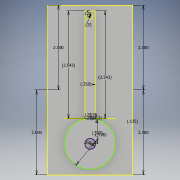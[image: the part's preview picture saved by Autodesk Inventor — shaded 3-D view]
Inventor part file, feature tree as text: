
AUTODESK INVENTOR PART (.ipt)
format: ipt  version: 2017 (Build 210142000, 142)  size: 172,032 bytes
history: native  units: in
note: dims shown in document units (in); Inventor stores cm internally (conversion verified against a paired STEP export)
features: sketch x12, extrude x5, hole x2, projected_geometry x2, plane x1
ambient origin geometry x8: Origin, YZ Plane, XZ Plane, XY Plane, X Axis, Y Axis, Z Axis, Center Point
bodies: Solid1 (feature_tree)
feature tree (22):
  extrude  "Extrusion1"  Depth=0.125in
  sketch  "Sketch2"  dims[d1=0.125in d2=0.0in d3=0.125in]
  plane  "Work Plane1"
  extrude  "Extrusion2"  Depth=0.25in
  extrude  "Extrusion3"  Depth=0.5in TaperAngle=0.0deg
  sketch  "Sketch6"  dims[d24=0.255in]
  hole  "Hole1"  [1 undecoded]
  hole  "Hole2"  [1 undecoded]
  extrude  "Extrusion6"  Depth=2.0in
  extrude  "Extrusion7"  Depth=2.0in
  sketch  "Sketch9"  dims[d40=0.125in d41=1.0in d42=0.0in]
  sketch  "Sketch10"  dims[d45=2.0in d46=2.0in]
  sketch  "Sketch11"  dims[d47=2.0in d48=2.0in]
  sketch  "Sketch12"  dims[d49=0.125in d50=0.0in]
  sketch  "Sketch13"  dims[d51=2.5427in]
  sketch  "Sketch14"  dims[d52=2.5427in d53=0.7275in d54=0.25in d55=0.5868in d56=0.125in d57=0.0132in]
  sketch  "Sketch3"  dims[d4=0.125in d6=0.25in]
  sketch  "Sketch4"  dims[d7=2.5295in d8=0.0in d9=0.5in d10=0.0in]
  sketch  "Sketch7"  dims[d25=0.255in d26=0.75in d27=0.375in d28=0.25in d29=0.5635in d30=1.0in d31=0.8108in]
  sketch  "Sketch8"  dims[d32=0.255in d33=0.75in d34=0.375in d35=0.25in d36=0.5635in d37=0.3125in d38=0.8108in d39=0.125in]
  projected_geometry  "Projected Loop1"
  projected_geometry  "Projected Loop2"
note: 2 required parameter values undecoded (feature->parameter linkage not recoverable at this tier; creation-order binding heuristic only, values carry confidence <= 0.55)
